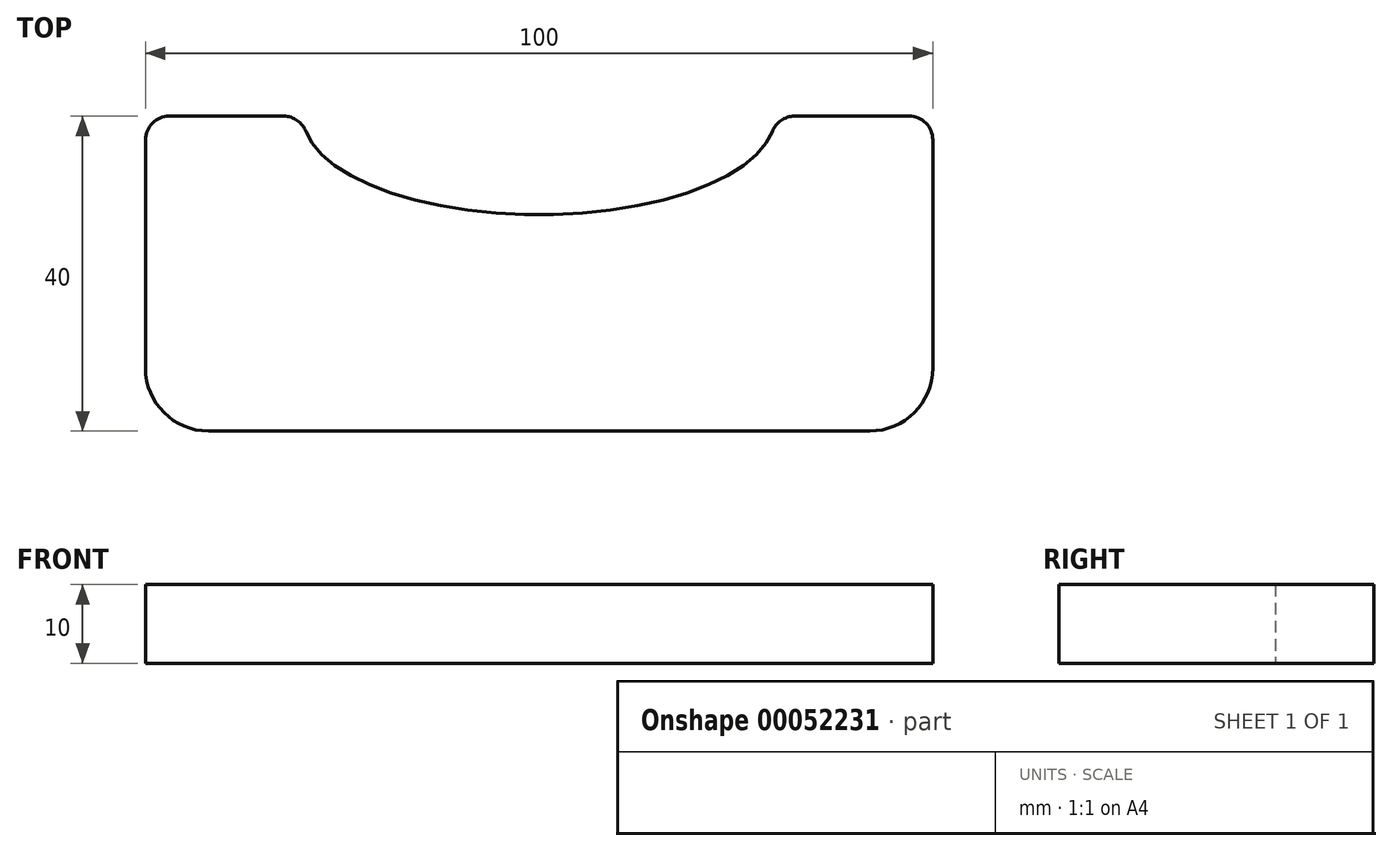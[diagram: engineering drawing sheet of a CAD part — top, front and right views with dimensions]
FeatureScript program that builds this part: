
annotation { "Feature Type Name" : "Feature", "Feature Type Description" : "" }
export const myFeature = defineFeature(function(context is Context, id is Id, definition is map)
    precondition{}
    {
        {
            var Q0;
            Q0=qCreatedBy(makeId("Top.planeOp"),FACE);
            var sketch = newSketch(context, id + "F0", { "sketchPlane" : qUnion([Q0])});
            skLineSegment(sketch, "E0.bottom", {"start": v(-36.73, -47) * mm, "end": v(63.27, -47) * mm});
            skLineSegment(sketch, "E0.top", {"start": v(-36.73, -87) * mm, "end": v(63.27, -87) * mm});
            skLineSegment(sketch, "E0.left", {"start": v(-36.73, -47) * mm, "end": v(-36.73, -87) * mm});
            skLineSegment(sketch, "E0.right", {"start": v(63.27, -47) * mm, "end": v(63.27, -87) * mm});
            skSolve(sketch);
        }
        {
            var Q0;
            Q0 = qSketchRegion(id + "F0", true);
            extrude(context, id + "F1", {"entities" : qUnion([Q0]), "depth" : 10 * mm});
        }
        {
            var Q0;
            Q0=makeQuery(id+"F1.opExtrude","CAP_FACE",FACE,{"disambiguationData":[OSD([sQuery(id+"F0.wireOp",EDGE,"E0.bottom"),sQuery(id+"F0.wireOp",EDGE,"E0.top"),sQuery(id+"F0.wireOp",EDGE,"E0.left"),sQuery(id+"F0.wireOp",EDGE,"E0.right")])],"isStart":false});
            var sketch = newSketch(context, id + "F2", { "sketchPlane" : qUnion([Q0])});
            skEllipse(sketch, "E1", {"center": v(13.27, -47) * mm, "majorRadius": 30 * mm, "minorRadius": 12.5 * mm, "majorAxis": v(1, 0)});
            skSolve(sketch);
        }
        {
            var Q0;
            Q0 = qSketchRegion(id + "F2", true);
            extrude(context, id + "F3", {"entities" : qUnion([Q0]), "operationType" : NewBodyOperationType.REMOVE, "endBound" : BoundingType.THROUGH_ALL, "oppositeDirection" : true, "depth" : 25 * mm});
        }
        {
            var Q0;
            Q0=makeQuery(id+"F1.opExtrude","SWEPT_EDGE",EDGE,{"disambiguationData":[OSD([sQuery(id+"F0.wireOp",EDGE,"E0.top"),sQuery(id+"F0.wireOp",EDGE,"E0.left")])]});
            var Q1;
            Q1=makeQuery(id+"F1.opExtrude","SWEPT_EDGE",EDGE,{"disambiguationData":[OSD([sQuery(id+"F0.wireOp",EDGE,"E0.top"),sQuery(id+"F0.wireOp",EDGE,"E0.right")])]});
            fillet(context, id + "F4", {"entities" : qUnion([Q0, Q1]), "radius" : 8 * mm, "tangentPropagation" : true, "allowEdgeOverflow" : false});
        }
        {
            var Q0;
            Q0=makeQuery(id+"F1.opExtrude","SWEPT_EDGE",EDGE,{"disambiguationData":[OSD([sQuery(id+"F0.wireOp",EDGE,"E0.bottom"),sQuery(id+"F0.wireOp",EDGE,"E0.right")])]});
            var Q1;
            Q1=makeQuery(id+"F3.boolean.opBoolean","INTERSECT",EDGE,{"disambiguationData":[OD(1.0)],"derivedFrom":[makeQuery(id+"F1.opExtrude","SWEPT_FACE",FACE,{"disambiguationData":[OSD([sQuery(id+"F0.wireOp",EDGE,"E0.bottom")])]}),makeQuery(id+"F3.opExtrude","SWEPT_FACE",FACE,{"disambiguationData":[OSD([sQuery(id+"F2.wireOp",EDGE,"E1")])]})]});
            var Q2;
            Q2=makeQuery(id+"F3.boolean.opBoolean","INTERSECT",EDGE,{"disambiguationData":[OD(0.0)],"derivedFrom":[makeQuery(id+"F1.opExtrude","SWEPT_FACE",FACE,{"disambiguationData":[OSD([sQuery(id+"F0.wireOp",EDGE,"E0.bottom")])]}),makeQuery(id+"F3.opExtrude","SWEPT_FACE",FACE,{"disambiguationData":[OSD([sQuery(id+"F2.wireOp",EDGE,"E1")])]})]});
            var Q3;
            Q3=makeQuery(id+"F1.opExtrude","SWEPT_EDGE",EDGE,{"disambiguationData":[OSD([sQuery(id+"F0.wireOp",EDGE,"E0.bottom"),sQuery(id+"F0.wireOp",EDGE,"E0.left")])]});
            fillet(context, id + "F5", {"entities" : qUnion([Q0, Q1, Q2, Q3]), "radius" : 3 * mm, "tangentPropagation" : true, "allowEdgeOverflow" : false});
        }
    });
